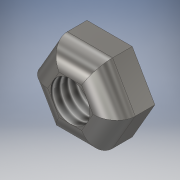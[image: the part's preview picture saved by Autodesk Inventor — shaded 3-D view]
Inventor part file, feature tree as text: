
AUTODESK INVENTOR PART (.ipt)
format: ipt  version: 2018 (Build 220112000, 112)  size: 133,120 bytes
history: native  units: in
note: dims shown in document units (in); Inventor stores cm internally (conversion verified against a paired STEP export)
features: extrude x2, sketch x2, thread x1, fillet x1
ambient origin geometry x8: Origin, YZ Plane, XZ Plane, XY Plane, X Axis, Y Axis, Z Axis, Center Point
bodies: Solid1 (feature_tree)
feature tree (6):
  extrude  "Extrusion1"  Depth=0.25in TaperAngle=0.0deg
  extrude  "Extrusion2"  Depth=0.25in TaperAngle=0.0deg
  thread  "Thread1"  [1 undecoded]
  fillet  "Fillet1"  Radius=0.125in
  sketch  "Sketch1"  dims[d0=0.5in d1=0.25in d2=0.0in]
  sketch  "Sketch2"  dims[d3=0.25in d4=0.25in d5=0.0in d6=1.0in d7=0.0in d8=0.125in]
note: 1 required parameter value undecoded (feature->parameter linkage not recoverable at this tier; creation-order binding heuristic only, values carry confidence <= 0.55)
